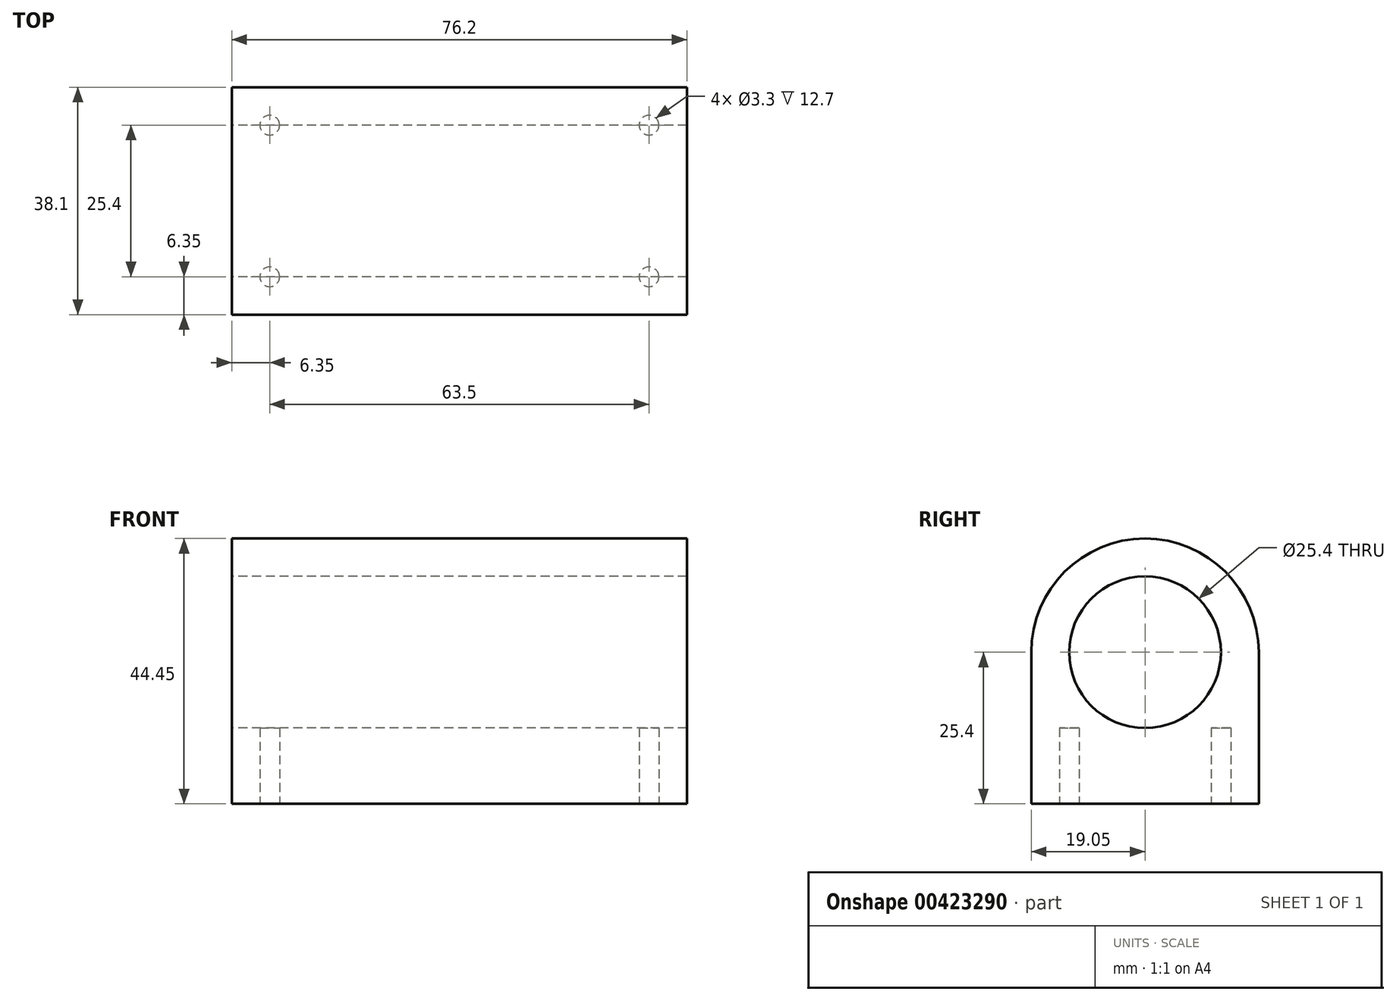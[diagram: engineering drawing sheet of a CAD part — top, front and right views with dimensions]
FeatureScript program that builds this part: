
annotation { "Feature Type Name" : "Feature", "Feature Type Description" : "" }
export const myFeature = defineFeature(function(context is Context, id is Id, definition is map)
    precondition{}
    {
        {
            var Q0;
            Q0=qCreatedBy(makeId("Right.planeOp"),FACE);
            var sketch = newSketch(context, id + "F0", { "sketchPlane" : qUnion([Q0])});
            skCircle(sketch, "E0", {"center": v(0, 0) * mm, "radius": 12.7 * mm});
            skArc(sketch, "E1", {"start": v(19.05, 0) * mm, "mid": v(0, 19.05) * mm, "end": v(-19.05, 0) * mm});
            skLineSegment(sketch, "E2.top", {"start": v(-19.05, -25.4) * mm, "end": v(19.05, -25.4) * mm});
            skLineSegment(sketch, "E2.left", {"start": v(-19.05, 0) * mm, "end": v(-19.05, -25.4) * mm});
            skLineSegment(sketch, "E2.right", {"start": v(19.05, 0) * mm, "end": v(19.05, -25.4) * mm});
            skSolve(sketch);
        }
        {
            var Q0;
            Q0 = qSketchRegion(id + "F0", true);
            extrude(context, id + "F1", {"entities" : qUnion([Q0]), "endBound" : BoundingType.SYMMETRIC, "depth" : 76.2 * mm});
        }
        {
            var Q0;
            Q0=makeQuery(id+"F1.opExtrude","SWEPT_FACE",FACE,{"disambiguationData":[OSD([sQuery(id+"F0.wireOp",EDGE,"E2.top")])]});
            var sketch = newSketch(context, id + "F2", { "sketchPlane" : qUnion([Q0])});
            skLineSegment(sketch, "E3.bottom", {"start": v(-31.75, 12.7) * mm, "end": v(31.75, 12.7) * mm, "construction": true});
            skLineSegment(sketch, "E3.top", {"start": v(-31.75, -12.7) * mm, "end": v(31.75, -12.7) * mm, "construction": true});
            skLineSegment(sketch, "E3.left", {"start": v(-31.75, 12.7) * mm, "end": v(-31.75, -12.7) * mm, "construction": true});
            skLineSegment(sketch, "E3.right", {"start": v(31.75, 12.7) * mm, "end": v(31.75, -12.7) * mm, "construction": true});
            skCircle(sketch, "E4", {"center": v(-31.75, 12.7) * mm, "radius": 1.65 * mm});
            skCircle(sketch, "E5", {"center": v(-31.75, -12.7) * mm, "radius": 1.65 * mm});
            skCircle(sketch, "E6", {"center": v(31.75, -12.7) * mm, "radius": 1.65 * mm});
            skCircle(sketch, "E7", {"center": v(31.75, 12.7) * mm, "radius": 1.65 * mm});
            skSolve(sketch);
        }
        {
            var Q0;
            Q0=makeQuery(id+"F2.imprint","IMPRINT",FACE,{"disambiguationData":[TD([[makeQuery(id+"F2.imprint","IMPRINT",EDGE,{"derivedFrom":sQuery(id+"F2.wireOp",EDGE,"E4")}),1.0]])]});
            var Q1;
            Q1=makeQuery(id+"F2.imprint","IMPRINT",FACE,{"disambiguationData":[TD([[makeQuery(id+"F2.imprint","IMPRINT",EDGE,{"derivedFrom":sQuery(id+"F2.wireOp",EDGE,"E5")}),1.0]])]});
            var Q2;
            Q2=makeQuery(id+"F2.imprint","IMPRINT",FACE,{"disambiguationData":[TD([[makeQuery(id+"F2.imprint","IMPRINT",EDGE,{"derivedFrom":sQuery(id+"F2.wireOp",EDGE,"E7")}),1.0]])]});
            var Q3;
            Q3=makeQuery(id+"F2.imprint","IMPRINT",FACE,{"disambiguationData":[TD([[makeQuery(id+"F2.imprint","IMPRINT",EDGE,{"derivedFrom":sQuery(id+"F2.wireOp",EDGE,"E6")}),1.0]])]});
            extrude(context, id + "F3", {"entities" : qUnion([Q0, Q1, Q2, Q3]), "operationType" : NewBodyOperationType.REMOVE, "oppositeDirection" : true, "depth" : 12.7 * mm});
        }
    });
